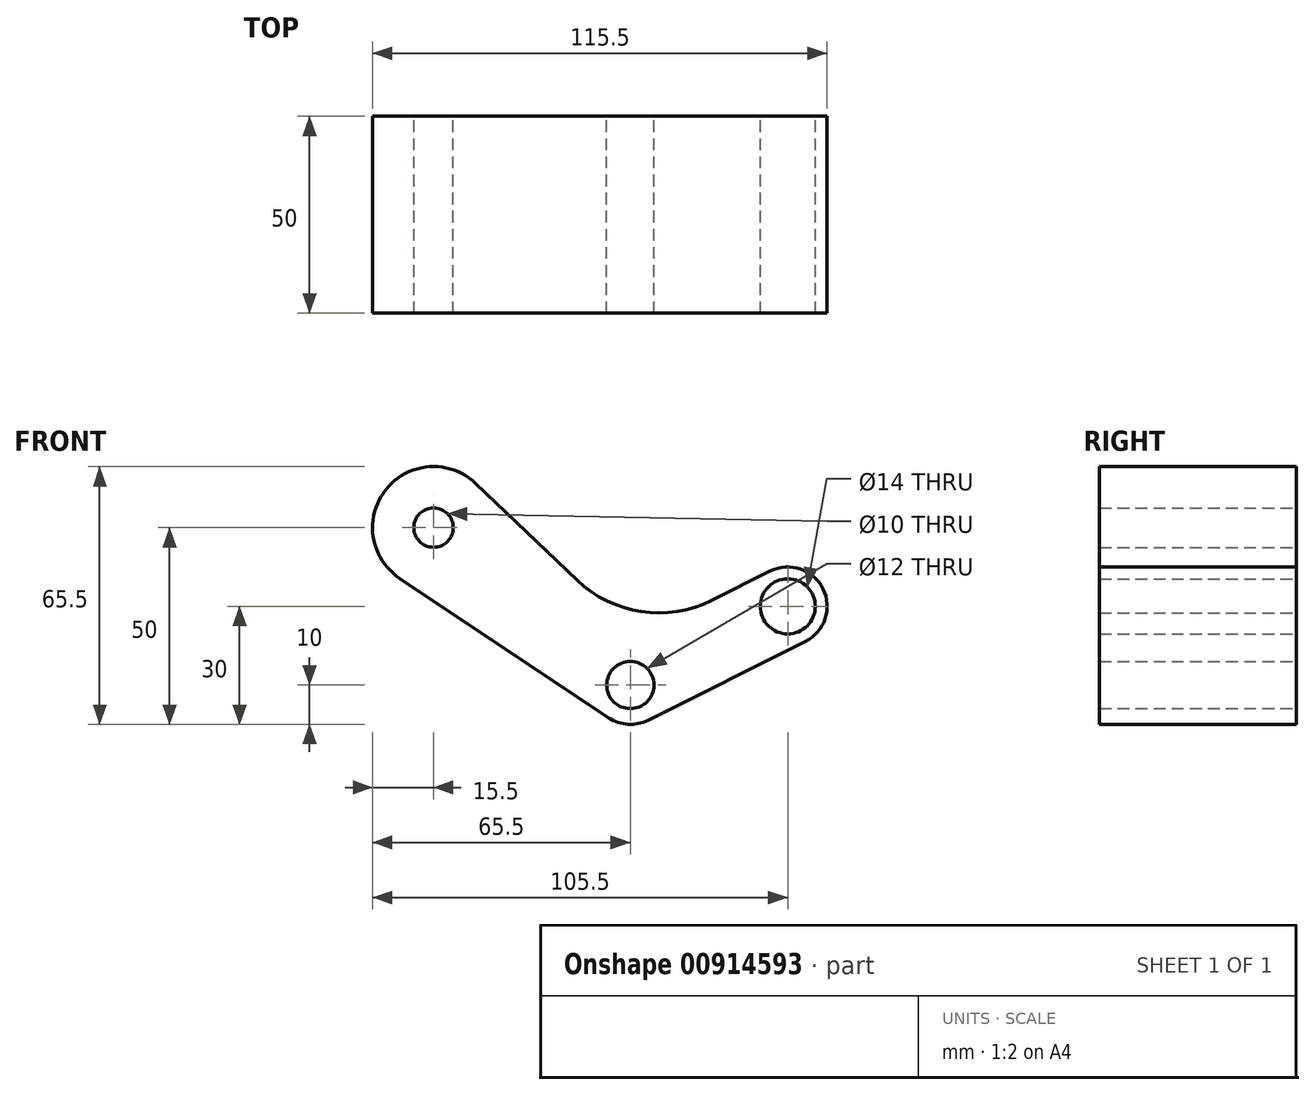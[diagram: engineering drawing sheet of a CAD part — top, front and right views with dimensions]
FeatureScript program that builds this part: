
annotation { "Feature Type Name" : "Feature", "Feature Type Description" : "" }
export const myFeature = defineFeature(function(context is Context, id is Id, definition is map)
    precondition{}
    {
        {
            var Q0;
            Q0=qCreatedBy(makeId("Front.planeOp"),FACE);
            var sketch = newSketch(context, id + "F0", { "sketchPlane" : qUnion([Q0])});
            skCircle(sketch, "E0", {"center": v(0, 0) * mm, "radius": 10 * mm});
            skCircle(sketch, "E1", {"center": v(0, 0) * mm, "radius": 6 * mm});
            skCircle(sketch, "E2", {"center": v(40, 20) * mm, "radius": 10 * mm});
            skCircle(sketch, "E3", {"center": v(40, 20) * mm, "radius": 7 * mm});
            skCircle(sketch, "E4", {"center": v(-50, 40) * mm, "radius": 15.5 * mm});
            skCircle(sketch, "E5", {"center": v(-50, 40) * mm, "radius": 5 * mm});
            skLineSegment(sketch, "E6", {"start": v(-58.6, 27.1) * mm, "end": v(-5.55, -8.32) * mm});
            skLineSegment(sketch, "E7", {"start": v(4.47, -8.94) * mm, "end": v(44.47, 11.06) * mm});
            skLineSegment(sketch, "E8", {"start": v(-39.3, 51.22) * mm, "end": v(-13.48, 26.61) * mm});
            skLineSegment(sketch, "E9", {"start": v(20.63, 21.5) * mm, "end": v(35.53, 28.94) * mm});
            skPoint(sketch, "E10.visualSharp", {"position": v(1.78, 12.07) * mm});
            skArc(sketch, "E10.filletArc", {"start": v(-13.48, 26.61) * mm, "mid": v(2.77, 18.66) * mm, "end": v(20.63, 21.5) * mm});
            skSolve(sketch);
        }
        {
            var Q0;
            Q0=makeQuery(id+"F0.imprint","IMPRINT",FACE,{"disambiguationData":[TD([[makeQuery(id+"F0.imprint","IMPRINT",EDGE,{"derivedFrom":sQuery(id+"F0.wireOp",EDGE,"E5")}),-1.0]])]});
            var Q1;
            {var subQ0=sQuery(id+"F0.wireOp",EDGE,"E6");Q1=makeQuery(id+"F0.imprint","IMPRINT",FACE,{"disambiguationData":[TD([[makeQuery(id+"F0.imprint","IMPRINT",EDGE,{"derivedFrom":subQ0}),1.0]])]});}
            var Q2;
            Q2=makeQuery(id+"F0.imprint","IMPRINT",FACE,{"disambiguationData":[TD([[makeQuery(id+"F0.imprint","IMPRINT",EDGE,{"derivedFrom":sQuery(id+"F0.wireOp",EDGE,"E1")}),-1.0]])]});
            var Q3;
            Q3=makeQuery(id+"F0.imprint","IMPRINT",FACE,{"disambiguationData":[TD([[makeQuery(id+"F0.imprint","IMPRINT",EDGE,{"derivedFrom":sQuery(id+"F0.wireOp",EDGE,"E3")}),-1.0]])]});
            extrude(context, id + "F1", {"entities" : qUnion([Q0, Q1, Q2, Q3]), "endBound" : BoundingType.SYMMETRIC, "depth" : 50 * mm, "offsetDistance" : 25 * mm});
        }
    });
